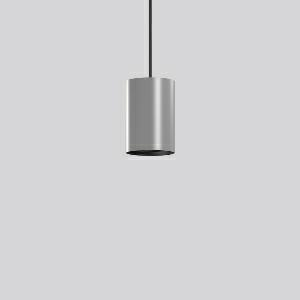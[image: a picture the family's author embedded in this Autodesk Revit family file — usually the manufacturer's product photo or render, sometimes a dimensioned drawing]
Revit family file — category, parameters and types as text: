
# Revit family: deecos_p_maxi_911530_004_3_edcf
name_source: partatom
category: Lighting Fixtures
units: mm (PartAtom-declared; Revit-internal decimal feet)

## family parameters
Cut with Voids When Loaded = No
Host = Face
Light Source = No
Part Type = Normal
Room Calculation Point = No
Round Connector Dimension = Use Diameter
Shared = No

## types (1)
- DEECOS P maxi (1 x LED Modul 935, 3400 lm, 3500)
    Apparent Load = 25 VA
    Approval mark = CE
    CIE Flux Codes = 100 100 100 100 100
    Color Rendering = 92
    Color Temperature = 3500
    Default Elevation = 1800 mm
    Description = Series: DEECOS P maxi
Cylindrical pendant luminaire. Housing: die-cast aluminium, powder-coated. Canopy made of powder-coated sheet steel with magnetic attachment. Optical assembly with reflector made of MIRO-Silver with 98% total light reflection for outstanding efficiency - can be changed without tools. Best colour rendering index Ra>90. Transparent suspension cable 2 m, can be shortened. High quality converter without flickering and stroboscopic effect. The following accessories can be mounted without use of tools: interchangeable lenses, honeycomb louvre, clear and frosted diffusers, white interchangeable plastic ring. Decorative recessed suspension set available as accessory. 
Colour: silver
Diameter: 123 mm
Height: 181 mm
Suspension length: 2000 mm
Lamp: LED
Socket: without socket
Colour temperature: 3500K
Colour rendering index (CRI): 92
System power: 25 W
Rated luminous flux: 3400 lm
Luminous efficiency: 136 lm/W
Control gear: Regulated power supply
Protection class: I
Type of protection: IP 20
    Height = 181 mm
    Lamp = 1 x LED Modul 935
    Lamp Light Flux = 3400 lm
    Lamp count = 1
    Length = 123 mm
    Lifetime = 50000 h
    Luminous efficacy = 136 lm/W
    Manufacturer = RZB
    ModVariant = No
    Model = 911530.004.3
    Mounting Place = Ceiling
    Mounting Type = Pendant
    Number of Poles = 1
    OnlyDefault = Yes
    Power Factor = 1
    Product Name = DEECOS P maxi
    Product group = Pendant luminaires
    ProductGroupID = 902
    Protection Class = Protection class I
    Protection Degree = IP 20
    RLX_Detail_Level = 1
    RLX_Emergency_Light_Flux = 0 lm
    RLX_Emergency_Type = 0
    RLX_Emergency_Type_DB = No
    RlxData = <blob elided: 35761 chars, md5=732d8b91>
    Socket = socket
    Standby Power = 0 W
    System Light Flux = 3400 lm
    System Power = 25 W
    Type Comments = Product without accessories
    Type Image = 911480.004.jpg
    URL = http://relux.com
    VarID = ---
    Voltage = 230 V
    Voltage Range = 220-240 V
    Weight = 0.00 kg
    Width = 0 mm  [stored 0 ft]

note: [stored X ft] marks values corroborated as IEEE doubles in the binary element streams (Revit-internal decimal feet)

## geometry (parser evidence)
native form markers: Blend x4, Sweep x10
no freeform markers — native parametric forms only
